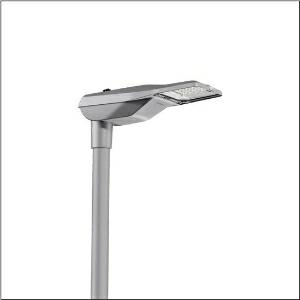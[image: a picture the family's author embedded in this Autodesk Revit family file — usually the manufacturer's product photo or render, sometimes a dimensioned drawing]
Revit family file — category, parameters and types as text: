
# Revit family: streetlight_sl_21_micro___st1_0ab_5xe1m33s08db_765d
name_source: partatom
category: Lighting Fixtures
units: mm (PartAtom-declared; Revit-internal decimal feet)

## family parameters
Cut with Voids When Loaded = No
Host = Face
Light Source = No
Part Type = Normal
Room Calculation Point = No
Round Connector Dimension = Use Diameter
Shared = No

## types (1)
- --- (1 x LED, 4500 lm, 39.1 W, 3000K)
    Apparent Load = 39 VA
    CIE Flux Codes = 38 73 97 100 100
    Color Rendering = 70
    Color Temperature = 3000K
    Default Elevation = 1800 mm
    Description = Streetlight SL 21 micro, mast luminaire, primary light control with lens, of PMMA, primary optical cover: cover, of toughened safety glass, transparent, light distribution: ST1.0aB, light emission: direct distribution, primary light characteristic: asymmetric, installation type: side-entry, post-top, LED, High Power LED, rated luminous flux: 4.500lm, luminous efficacy: 115lm/W, light colour: 730, colour temperature: 3000K, control gear: D4i, control: flexible luminous flux parameterisation, time-dependent luminous flux control, constant luminous flux control, overheat protection, pre-setting: logarithmic dimming characteristic, mains connection: 220..240V, AC, 50/60Hz, start of lifetime: 39W, end of service life: 41W, reduction: 18W, luminaire housing, of diecast aluminium, powder-coated, Siteco® metallic grey (DB 702S), corrosivity category C5 mid according to DIN EN ISO 12944, please order mast flange separately, inclination adjustable: 0°, 5°, 10°, 15°, sealing non-destructively replaceable, multi-level sealing system, length: 528mm, width: 235mm, height: 110mm, mast flange for spigot size: 42mm (side-entry): 5XC10008XM4, 60/48mm (side-entry/post-top): 5XC10108XM2, 76/60mm (side-entry/post-top): 5XC10108XM1, Smart Interface above, protection rating (complete): IP66, insulation class (complete): insulation class II (safety insulation), certification: CE, ENEC, ENEC+, VDE, impact resistance: IK10, permissible operating ambient temperature for outdoor applications: -40..+50°C, standard-compliant lighting for roads and squares, packaging unit: 1 piece

Light Distribution: ST1.0aB
    Height = 110 mm
    Lamp = 1 x LED
    Lamp Light Flux = 4500 lm
    Lamp Power = 39.1 W
    Lamp count = 1
    Length = 528 mm
    Luminous efficacy = 115 lm/W
    Manufacturer = Siteco
    ModVariant = No
    Model = 5XE1M33S08DB
    Number of Poles = 1
    OnlyDefault = Yes
    Power Factor = 1
    Product Name = Streetlight SL 21 micro | ST1.0aB
    Product group = mast luminaire | pylon top
    ProductGroupID = 6100
    Protection Class = Protection class II
    Protection Degree = IP 66
    RLX_Detail_Level = 1
    RLX_Emergency_Light_Flux = 0 lm
    RLX_Emergency_Type = 0
    RLX_Emergency_Type_DB = No
    RlxData = <blob elided: 98325 chars, md5=84f0cda6>
    Socket = socket
    Standby Power = 0 W
    System Light Flux = 4500 lm
    System Power = 39 W
    Type Comments = factory setting: luminous flux: 100 % | dim-lin: 254 | 765 mA
    Type Image = l_1277292.jpg
    URL = http://relux.com
    VarID = @adj_175457
    Voltage = 0 V
    Weight = 0.00 kg
    Width = 235 mm

## geometry (parser evidence)
native form markers: Blend x4, Sweep x10
no freeform markers — native parametric forms only
